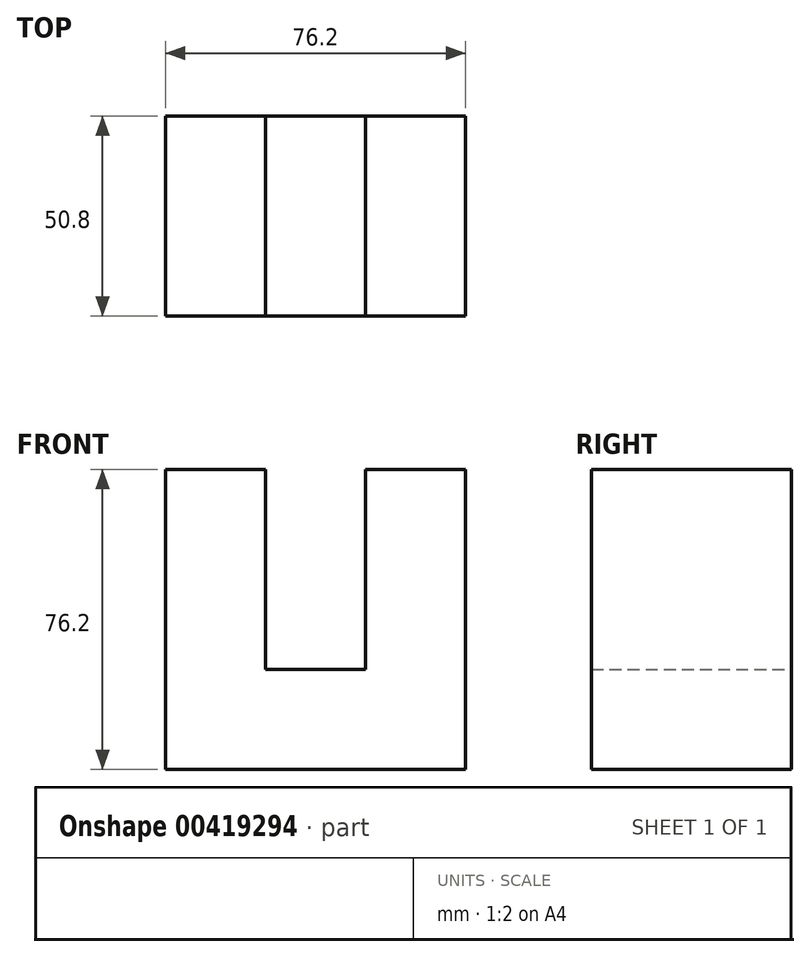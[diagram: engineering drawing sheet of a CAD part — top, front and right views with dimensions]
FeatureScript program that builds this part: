
annotation { "Feature Type Name" : "Feature", "Feature Type Description" : "" }
export const myFeature = defineFeature(function(context is Context, id is Id, definition is map)
    precondition{}
    {
        {
            var Q0;
            Q0=qCreatedBy(makeId("Front.planeOp"),FACE);
            var sketch = newSketch(context, id + "F0", { "sketchPlane" : qUnion([Q0])});
            skLineSegment(sketch, "E0", {"start": v(-33.38, 27.14) * mm, "end": v(-33.38, -49.06) * mm});
            skLineSegment(sketch, "E1", {"start": v(-33.38, -49.06) * mm, "end": v(42.82, -49.06) * mm});
            skLineSegment(sketch, "E2", {"start": v(42.82, -49.06) * mm, "end": v(42.82, 27.14) * mm});
            skLineSegment(sketch, "E3", {"start": v(42.82, 27.14) * mm, "end": v(17.42, 27.14) * mm});
            skLineSegment(sketch, "E4", {"start": v(17.42, 27.14) * mm, "end": v(17.42, -23.66) * mm});
            skLineSegment(sketch, "E5", {"start": v(17.42, -23.66) * mm, "end": v(-7.98, -23.66) * mm});
            skLineSegment(sketch, "E6", {"start": v(-7.98, -23.66) * mm, "end": v(-7.98, 27.14) * mm});
            skLineSegment(sketch, "E7", {"start": v(-7.98, 27.14) * mm, "end": v(-33.38, 27.14) * mm});
            skSolve(sketch);
        }
        {
            var Q0;
            Q0 = qSketchRegion(id + "F0", true);
            extrude(context, id + "F1", {"entities" : qUnion([Q0]), "depth" : 50.8 * mm});
        }
    });
